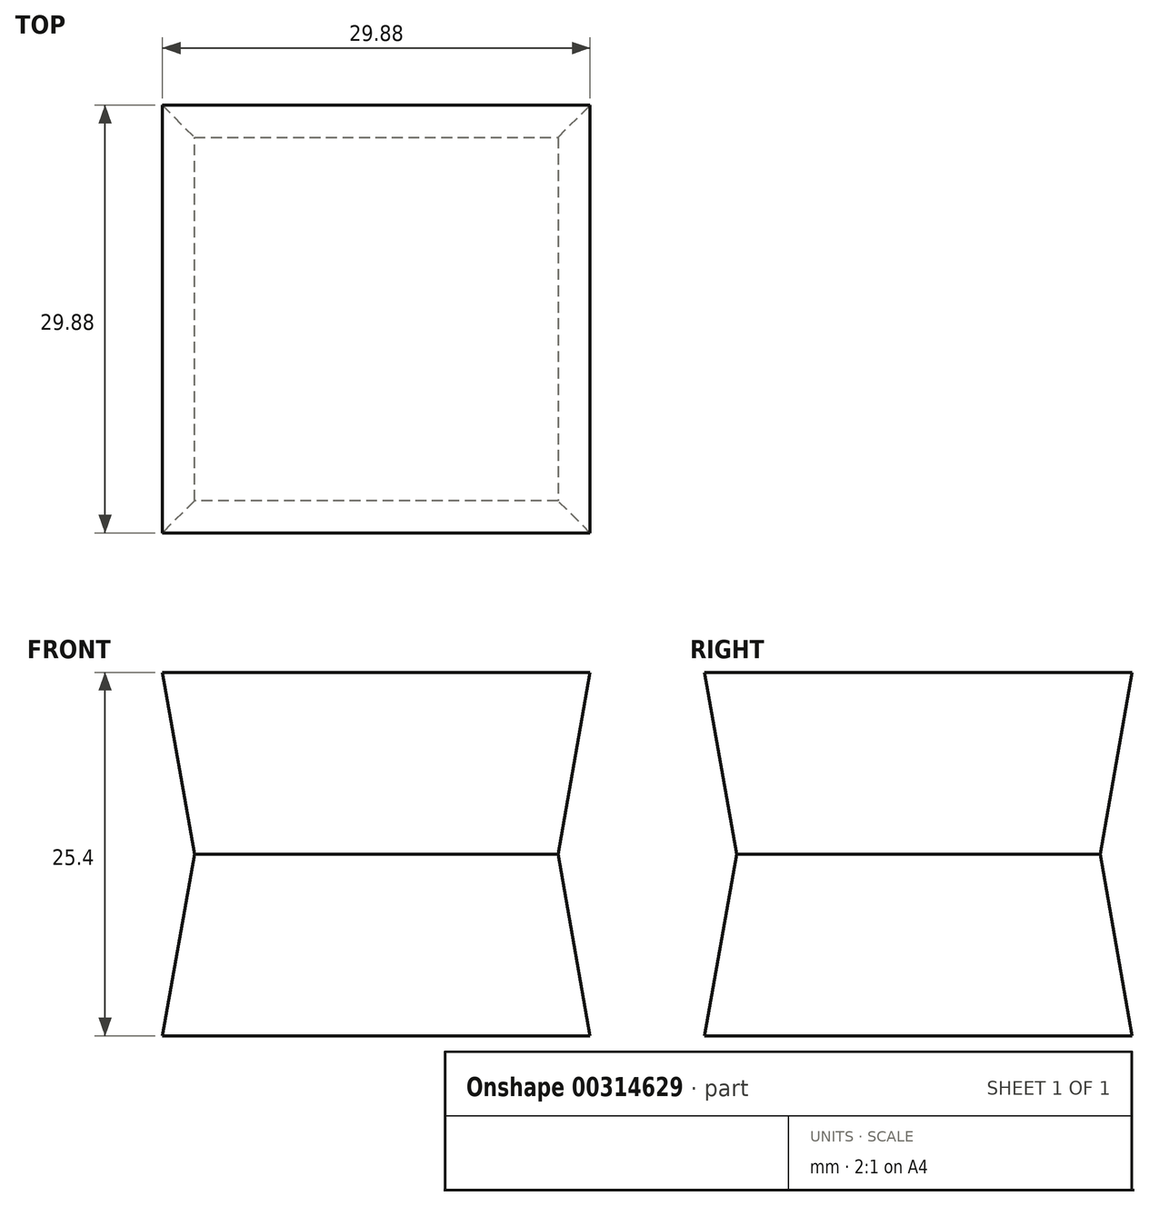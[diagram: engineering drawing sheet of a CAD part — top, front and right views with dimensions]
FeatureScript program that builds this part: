
annotation { "Feature Type Name" : "Feature", "Feature Type Description" : "" }
export const myFeature = defineFeature(function(context is Context, id is Id, definition is map)
    precondition{}
    {
        {
            var Q0;
            Q0=qCreatedBy(makeId("Top.planeOp"),FACE);
            var sketch = newSketch(context, id + "F0", { "sketchPlane" : qUnion([Q0])});
            skLineSegment(sketch, "E0.bottom", {"start": v(12.7, 12.7) * mm, "end": v(-12.7, 12.7) * mm});
            skLineSegment(sketch, "E0.top", {"start": v(12.7, -12.7) * mm, "end": v(-12.7, -12.7) * mm});
            skLineSegment(sketch, "E0.left", {"start": v(12.7, 12.7) * mm, "end": v(12.7, -12.7) * mm});
            skLineSegment(sketch, "E0.right", {"start": v(-12.7, 12.7) * mm, "end": v(-12.7, -12.7) * mm});
            skPoint(sketch, "E0.middle", {"position": v(0, 0) * mm});
            skSolve(sketch);
        }
        {
            var Q0;
            Q0 = qSketchRegion(id + "F0", true);
            extrude(context, id + "F1", {"entities" : qUnion([Q0]), "endBound" : BoundingType.SYMMETRIC, "depth" : 25.4 * mm, "hasDraft" : true, "draftAngle" : 10 * degree});
        }
    });
